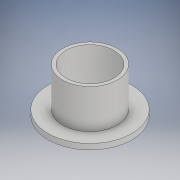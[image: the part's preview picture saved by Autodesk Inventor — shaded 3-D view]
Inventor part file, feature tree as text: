
AUTODESK INVENTOR PART (.ipt)
format: ipt  version: 2017 (Build 210142000, 142)  size: 112,128 bytes
history: native  units: mm
features: extrude x3, sketch x3, other x1
ambient origin geometry x8: Origin, YZ Plane, XZ Plane, XY Plane, X Axis, Y Axis, Z Axis, Center Point
bodies: Body1 (feature_tree)
feature tree (7):
  other  "Твердое тело1"
  extrude  "Выдавливание1"  Depth=15.0mm
  extrude  "Выдавливание2"  Depth=1.0mm TaperAngle=0.0deg
  extrude  "Выдавливание4"  Depth=9.8mm
  sketch  "Эскиз1"
  sketch  "Эскиз2"
  sketch  "Эскиз4"
